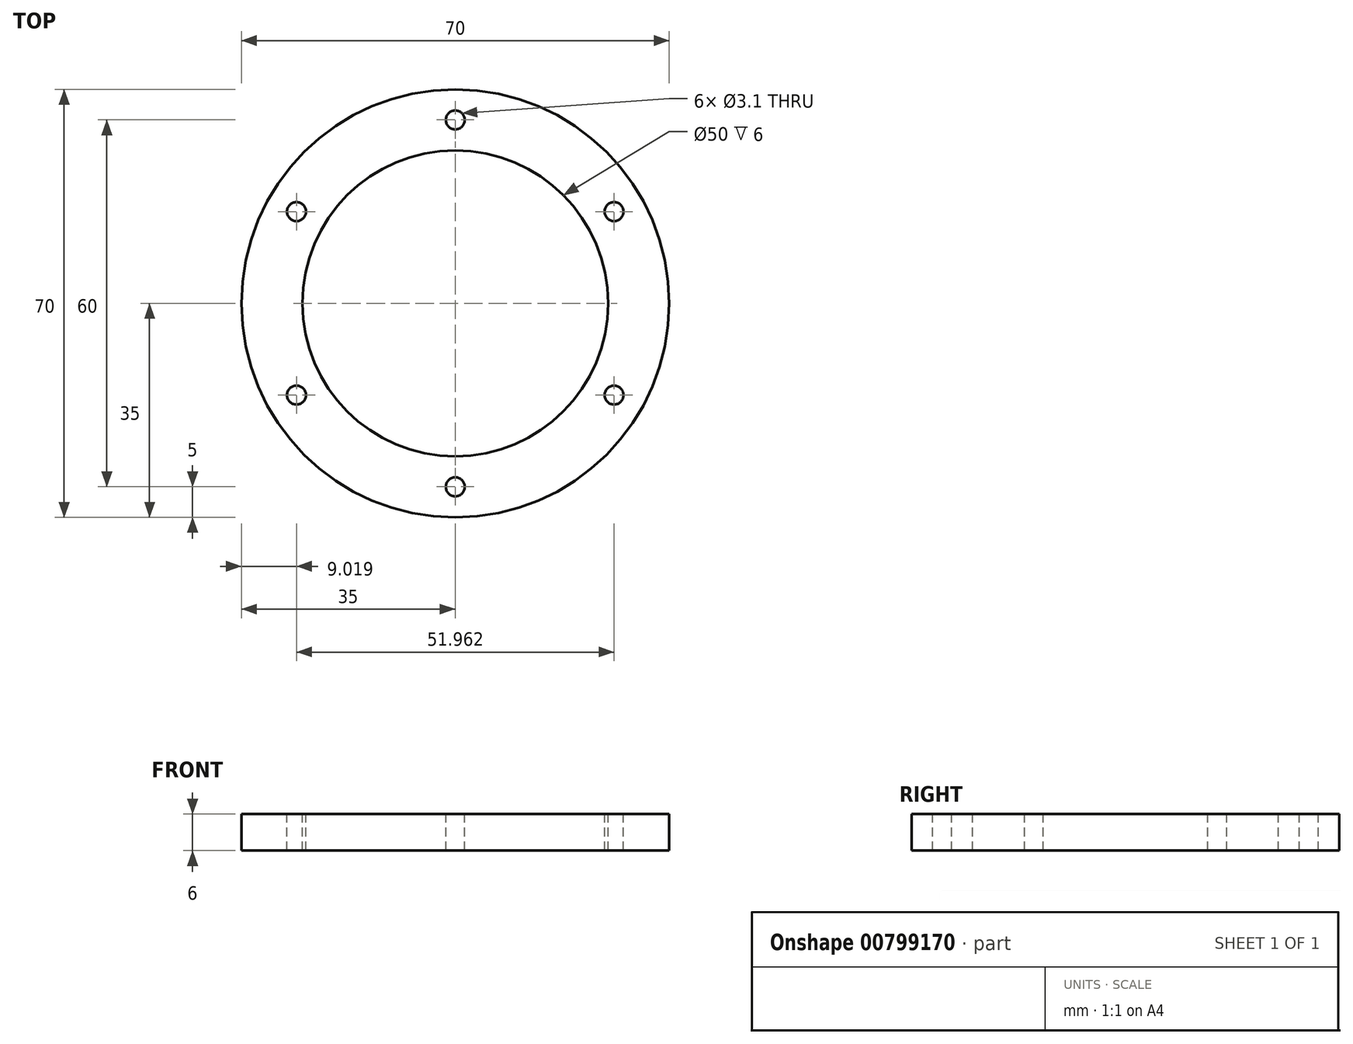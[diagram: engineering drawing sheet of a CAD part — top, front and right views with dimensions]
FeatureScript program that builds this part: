
annotation { "Feature Type Name" : "Feature", "Feature Type Description" : "" }
export const myFeature = defineFeature(function(context is Context, id is Id, definition is map)
    precondition{}
    {
        {
            var Q0;
            Q0=qCreatedBy(makeId("Top.planeOp"),FACE);
            var sketch = newSketch(context, id + "F0", { "sketchPlane" : qUnion([Q0])});
            skCircle(sketch, "E0", {"center": v(0, 0) * mm, "radius": 35 * mm});
            skSolve(sketch);
        }
        {
            var Q0;
            Q0=makeQuery(id+"F0.imprint","IMPRINT",FACE,{"disambiguationData":[TD([[makeQuery(id+"F0.imprint","IMPRINT",EDGE,{"derivedFrom":sQuery(id+"F0.wireOp",EDGE,"E0")}),1.0]])]});
            extrude(context, id + "F1", {"entities" : qUnion([Q0]), "depth" : 6 * mm, "offsetDistance" : 25 * mm});
        }
        {
            var Q0;
            Q0=makeQuery(id+"F1.opExtrude","CAP_FACE",FACE,{"disambiguationData":[OSD([sQuery(id+"F0.wireOp",EDGE,"E0")])],"isStart":false});
            var sketch = newSketch(context, id + "F2", { "sketchPlane" : qUnion([Q0])});
            skCircle(sketch, "E1", {"center": v(0, 30) * mm, "radius": 1.55 * mm});
            skCircle(sketch, "E2.1.0", {"center": v(-25.98, 15) * mm, "radius": 1.55 * mm});
            skCircle(sketch, "E2.2.0", {"center": v(-25.98, -15) * mm, "radius": 1.55 * mm});
            skPoint(sketch, "E2.center", {"position": v(0, 0) * mm});
            skCircle(sketch, "E3.1.3.0", {"center": v(0, -30) * mm, "radius": 1.55 * mm});
            skCircle(sketch, "E3.1.4.0", {"center": v(25.98, -15) * mm, "radius": 1.55 * mm});
            skCircle(sketch, "E3.1.5.0", {"center": v(25.98, 15) * mm, "radius": 1.55 * mm});
            skSolve(sketch);
        }
        {
            var Q0;
            Q0=makeQuery(id+"F2.imprint","IMPRINT",FACE,{"disambiguationData":[TD([[makeQuery(id+"F2.imprint","IMPRINT",EDGE,{"derivedFrom":sQuery(id+"F2.wireOp",EDGE,"E1")}),1.0]])]});
            var Q1;
            Q1=makeQuery(id+"F2.imprint","IMPRINT",FACE,{"disambiguationData":[TD([[makeQuery(id+"F2.imprint","IMPRINT",EDGE,{"derivedFrom":sQuery(id+"F2.wireOp",EDGE,"E2.1.0")}),1.0]])]});
            var Q2;
            Q2=makeQuery(id+"F2.imprint","IMPRINT",FACE,{"disambiguationData":[TD([[makeQuery(id+"F2.imprint","IMPRINT",EDGE,{"derivedFrom":sQuery(id+"F2.wireOp",EDGE,"E2.2.0")}),1.0]])]});
            var Q3;
            Q3=makeQuery(id+"F2.imprint","IMPRINT",FACE,{"disambiguationData":[TD([[makeQuery(id+"F2.imprint","IMPRINT",EDGE,{"derivedFrom":sQuery(id+"F2.wireOp",EDGE,"E3.1.5.0")}),1.0]])]});
            var Q4;
            Q4=makeQuery(id+"F2.imprint","IMPRINT",FACE,{"disambiguationData":[TD([[makeQuery(id+"F2.imprint","IMPRINT",EDGE,{"derivedFrom":sQuery(id+"F2.wireOp",EDGE,"E3.1.4.0")}),1.0]])]});
            var Q5;
            Q5=makeQuery(id+"F2.imprint","IMPRINT",FACE,{"disambiguationData":[TD([[makeQuery(id+"F2.imprint","IMPRINT",EDGE,{"derivedFrom":sQuery(id+"F2.wireOp",EDGE,"E3.1.3.0")}),1.0]])]});
            extrude(context, id + "F3", {"entities" : qUnion([Q0, Q1, Q2, Q3, Q4, Q5]), "operationType" : NewBodyOperationType.REMOVE, "endBound" : BoundingType.THROUGH_ALL, "oppositeDirection" : true, "depth" : 25 * mm, "offsetDistance" : 25 * mm});
        }
        {
            var Q0;
            Q0=makeQuery(id+"F1.opExtrude","CAP_FACE",FACE,{"disambiguationData":[OSD([sQuery(id+"F0.wireOp",EDGE,"E0")])],"isStart":false});
            var sketch = newSketch(context, id + "F4", { "sketchPlane" : qUnion([Q0])});
            skCircle(sketch, "E4", {"center": v(0, 0) * mm, "radius": 25 * mm});
            skSolve(sketch);
        }
        {
            var Q0;
            Q0=makeQuery(id+"F4.imprint","IMPRINT",FACE,{"disambiguationData":[TD([[makeQuery(id+"F4.imprint","IMPRINT",EDGE,{"derivedFrom":sQuery(id+"F4.wireOp",EDGE,"E4")}),1.0]])]});
            extrude(context, id + "F5", {"entities" : qUnion([Q0]), "operationType" : NewBodyOperationType.REMOVE, "endBound" : BoundingType.THROUGH_ALL, "oppositeDirection" : true, "depth" : 25 * mm, "offsetDistance" : 25 * mm});
        }
    });
